# Revit family: Celite_City_Coluna para Lavatório_20201
name_source: partatom
category: Plumbing Fixtures
revit_build: Autodesk Revit MEP 2014 (Build: 20131024_2115(x64)
units: mm (PartAtom-declared; Revit-internal decimal feet)

## types (8) — shared parameters
Assembly Code = D2010400
Celite: Categoria = Linhas Completas
Celite: Desenho Técnico = http://www.celite.com.br
Celite: Fabricante = Celite
Celite: Linha = City
Celite: Link do Produto = http://www.celite.com.br
Celite: Norma = ABNT NBR 15097-1: 2011 - Requisitos e métodos de ensaio
Celite: Produto = Colunas
Celite: Tipo = Colunas para lavatórios
Celite: Versão = Autodesk Revit MEP 2014
Desenvolvido por = ofcdesk
Manufacturer = Celite
Selo de Qualidade ofcdesk = Standard
URL = http://www.celite.com.br
zero-valued in all types: CWFU, Default Elevation, HWFU, WFU

## per-type parameters (varying)
| type | Celite: Cores Disponíveis | Celite: Código | Celite: Descrição | Coluna Int | Coluna Susp | Description | Model |
| Suspensa Branco - 20202 | Branco | 20202 | Coluna suspensa para lavatório cor branca 20202), linha City - Louças Celite | No | Yes | Coluna suspensa para lavatório cor branca 20202), linha City - Louças Celite | 20202 |
| Suspensa Pergamon - 20202 | Pergamon | 20202 | Coluna suspensa para lavatório cor pergamon (20202), linha City - Louças Celite | No | Yes | Coluna suspensa para lavatório cor pergamon (20202), linha City - Louças Celite | 20202 |
| Inteira Branco - 20201 | Branco | 20201 | Coluna para lavatório cor branca (20201), linha City - Louças Celite | Yes | No | Coluna para lavatório cor branca (20201), linha City - Louças Celite | 20201 |
| Inteira Pergamon - 20201 | Pergamon | 20201 | Coluna para lavatório cor pergamon (20201), linha City - Louças Celite | Yes | No | Coluna para lavatório cor pergamon (20201), linha City - Louças Celite | 20201 |
| Inteira Preto - 20201 | Preto | 20201 | Coluna para lavatório cor preta (20201), linha City - Louças Celite | Yes | No | Coluna para lavatório cor preta (20201), linha City - Louças Celite | 20201 |
| Inteira Cinza prata - 20201 | Cinza prata | 20201 | Coluna para lavatório cor cinza prata (20201), linha City - Louças Celite | Yes | No | Coluna para lavatório cor cinza prata (20201), linha City - Louças Celite | 20201 |
| Suspensa Preto - 20202 | Preto | 20202 | Coluna suspensa para lavatório cor preta (20202), linha City - Louças Celite | No | Yes | Coluna suspensa para lavatório cor preta (20202), linha City - Louças Celite | 20202 |
| Suspensa Cinza prata - 20202 | Cinza prata | 20202 | Coluna suspensa para lavatório cor cinza prata (20202), linha City - Louças Celite | No | Yes | Coluna suspensa para lavatório cor cinza prata (20202), linha City - Louças Celite | 20202 |

## geometry (parser evidence)
native form markers: Blend x2, Sweep x1
no freeform markers — native parametric forms only
